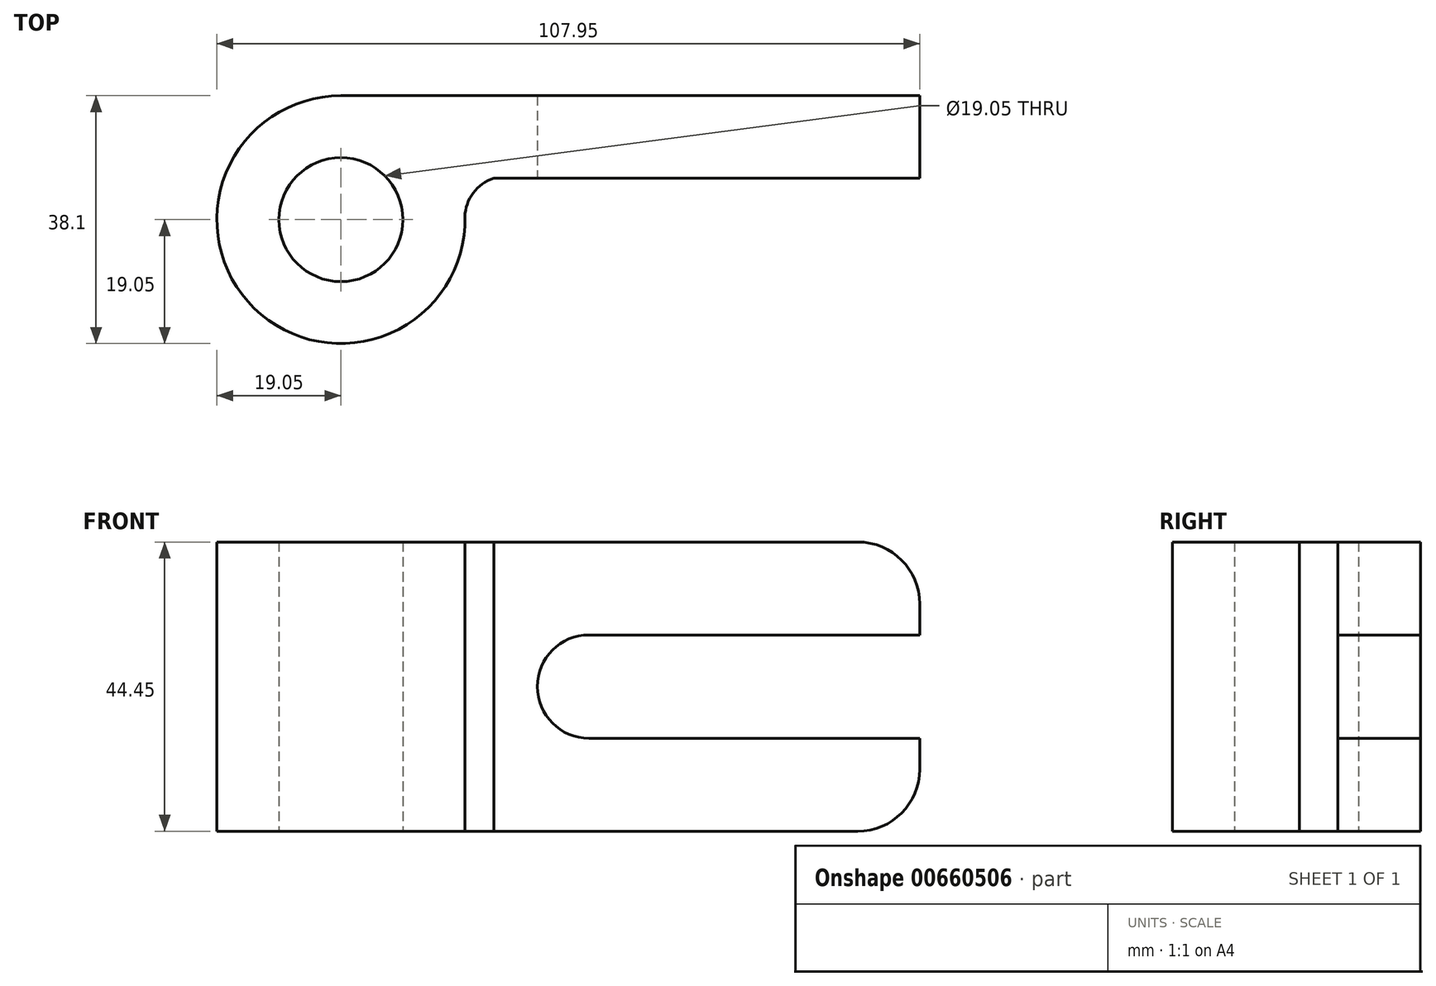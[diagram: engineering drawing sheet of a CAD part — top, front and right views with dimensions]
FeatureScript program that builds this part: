
annotation { "Feature Type Name" : "Feature", "Feature Type Description" : "" }
export const myFeature = defineFeature(function(context is Context, id is Id, definition is map)
    precondition{}
    {
        {
            var Q0;
            Q0=qCreatedBy(makeId("Top.planeOp"),FACE);
            var sketch = newSketch(context, id + "F0", { "sketchPlane" : qUnion([Q0])});
            skArc(sketch, "E0", {"start": v(0, 19.05) * mm, "mid": v(-13.31, -13.63) * mm, "end": v(19.04, 0.44) * mm});
            skLineSegment(sketch, "E1", {"start": v(0, 19.05) * mm, "end": v(88.9, 19.05) * mm});
            skLineSegment(sketch, "E2", {"start": v(88.9, 19.05) * mm, "end": v(88.9, 6.35) * mm});
            skLineSegment(sketch, "E3", {"start": v(88.9, 6.35) * mm, "end": v(23.48, 6.35) * mm});
            skArc(sketch, "E4", {"start": v(27.31, 6.35) * mm, "mid": v(21.52, 5.33) * mm, "end": v(19.05, 0) * mm});
            skCircle(sketch, "E5", {"center": v(0, 0) * mm, "radius": 9.53 * mm});
            skSolve(sketch);
        }
        {
            var Q0;
            Q0 = qSketchRegion(id + "F0", true);
            extrude(context, id + "F1", {"entities" : qUnion([Q0]), "depth" : 44.45 * mm, "offsetDistance" : 25.4 * mm});
        }
        {
            var Q0;
            Q0=makeQuery(id+"F1.opExtrude","SWEPT_FACE",FACE,{"disambiguationData":[OSD([sQuery(id+"F0.wireOp",EDGE,"E3")])]});
            var sketch = newSketch(context, id + "F2", { "sketchPlane" : qUnion([Q0])});
            skLineSegment(sketch, "E6", {"start": v(88.9, 44.45) * mm, "end": v(88.9, 30.16) * mm});
            skLineSegment(sketch, "E7", {"start": v(88.9, 0) * mm, "end": v(88.9, 14.29) * mm});
            skLineSegment(sketch, "E8", {"start": v(88.9, 14.29) * mm, "end": v(38.1, 14.29) * mm});
            skLineSegment(sketch, "E9", {"start": v(88.9, 30.16) * mm, "end": v(38.1, 30.16) * mm});
            skArc(sketch, "E10", {"start": v(38.1, 30.16) * mm, "mid": v(30.16, 22.22) * mm, "end": v(38.1, 14.29) * mm});
            skPoint(sketch, "E11", {"position": v(79.38, 34.93) * mm});
            skPoint(sketch, "E12", {"position": v(79.38, 9.53) * mm});
            skArc(sketch, "E13", {"start": v(79.38, 0) * mm, "mid": v(86.11, 2.79) * mm, "end": v(88.9, 9.53) * mm});
            skArc(sketch, "E14", {"start": v(88.9, 34.93) * mm, "mid": v(86.11, 41.66) * mm, "end": v(79.38, 44.45) * mm});
            skSolve(sketch);
        }
        {
            var Q0;
            Q0 = qSketchRegion(id + "F2", true);
            var Q1;
            {var subQ0=sQuery(id+"F2.wireOp",EDGE,"E8");Q1=makeQuery(id+"F2.imprint","IMPRINT",FACE,{"disambiguationData":[TD([[makeQuery(id+"F2.imprint","IMPRINT",EDGE,{"derivedFrom":subQ0}),-1.0]])]});}
            var Q2;
            {var subQ0=sQuery(id+"F2.wireOp",EDGE,"E6");var subQ1=makeQuery(id+"F1.opExtrude","CAP_EDGE",EDGE,{"disambiguationData":[OSD([sQuery(id+"F0.wireOp",EDGE,"E3")])],"isStart":false});var subQ2=makeQuery(id+"F2.imprint","INTERSECT",VERTEX,{"derivedFrom":[subQ1,subQ0]});Q2=makeQuery(id+"F2.imprint","IMPRINT",FACE,{"disambiguationData":[TD([[makeQuery(id+"F2.imprint","IMPRINT",EDGE,{"disambiguationData":[TD([[subQ2,-1.0]])],"derivedFrom":subQ0}),-1.0]])]});}
            var Q3;
            {var subQ3=sQuery(id+"F2.wireOp",EDGE,"E13");Q3=makeQuery(id+"F2.imprint","IMPRINT",FACE,{"disambiguationData":[TD([[makeQuery(id+"F2.imprint","IMPRINT",EDGE,{"derivedFrom":subQ3}),-1.0]])]});}
            extrude(context, id + "F3", {"entities" : qUnion([Q0, Q1, Q2, Q3]), "operationType" : NewBodyOperationType.REMOVE, "oppositeDirection" : true, "depth" : 25.4 * mm, "offsetDistance" : 25.4 * mm});
        }
    });
